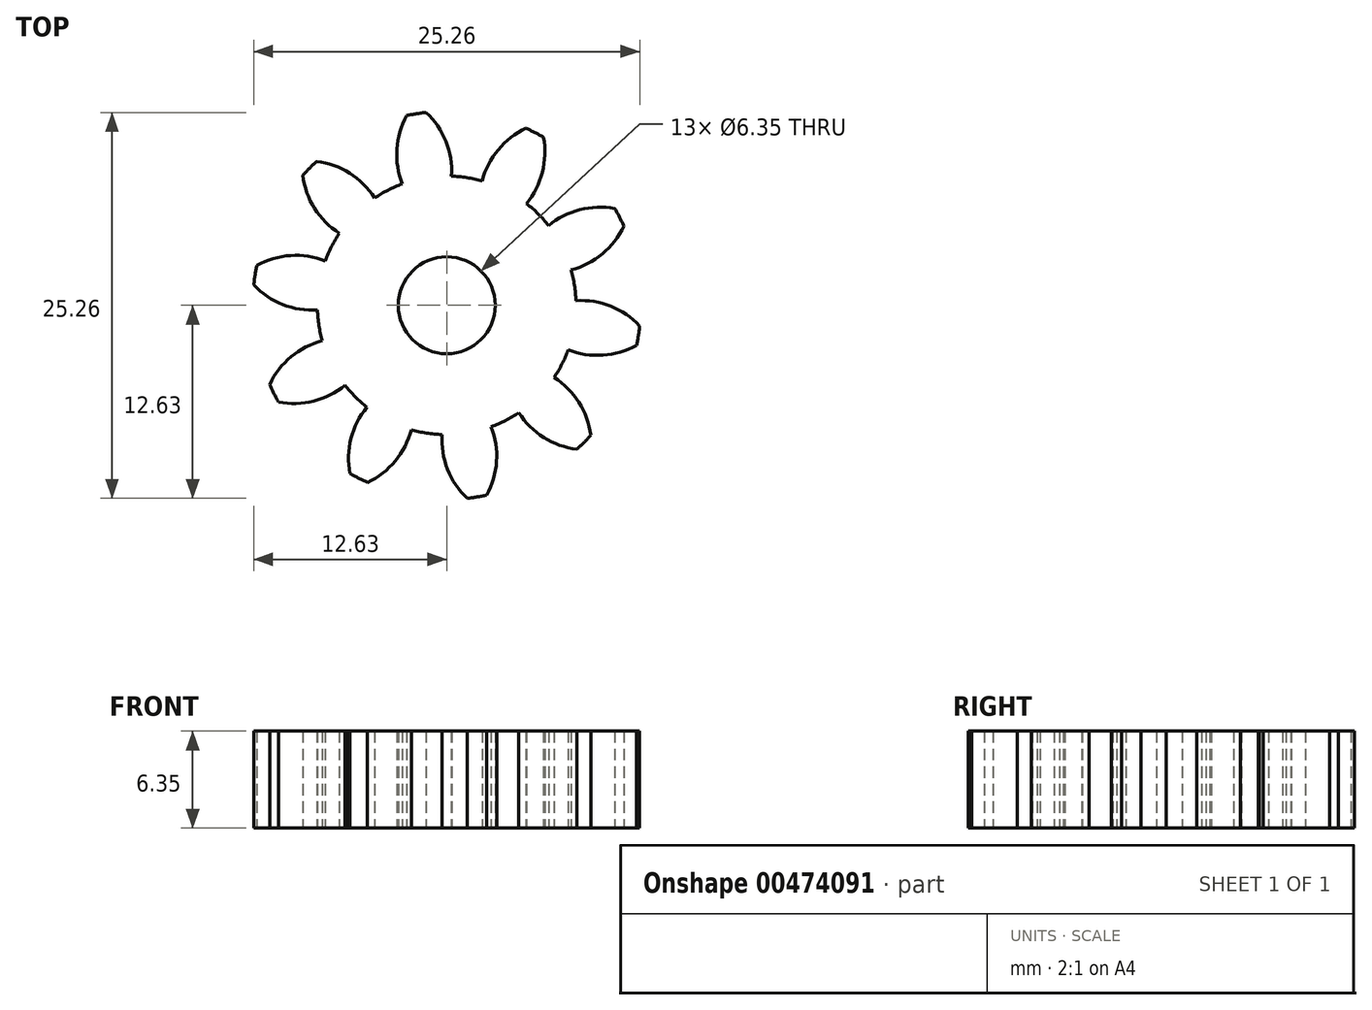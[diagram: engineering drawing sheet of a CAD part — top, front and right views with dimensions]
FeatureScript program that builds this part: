
annotation { "Feature Type Name" : "Feature", "Feature Type Description" : "" }
export const myFeature = defineFeature(function(context is Context, id is Id, definition is map)
    precondition{}
    {
        {
            var Q0;
            Q0=qCreatedBy(makeId("Top.planeOp"),FACE);
            var sketch = newSketch(context, id + "F0", { "sketchPlane" : qUnion([Q0])});
            skCircle(sketch, "E0", {"center": v(0, 0) * mm, "radius": 3.18 * mm});
            skCircle(sketch, "E1", {"center": v(0, 0) * mm, "radius": 8.47 * mm});
            skCircle(sketch, "E2", {"center": v(0, 0) * mm, "radius": 10.58 * mm, "construction": true});
            skCircle(sketch, "E3", {"center": v(0, 0) * mm, "radius": 12.7 * mm, "construction": true});
            skLineSegment(sketch, "E4", {"start": v(0, 0) * mm, "end": v(0, 10.58) * mm, "construction": true});
            skLineSegment(sketch, "E5", {"start": v(0, 10.58) * mm, "end": v(-16.23, 10.58) * mm, "construction": true});
            skLineSegment(sketch, "E6", {"start": v(0, 10.58) * mm, "end": v(-16.16, 4.7) * mm, "construction": true});
            skArc(sketch, "E7", {"start": v(0.3, 8.46) * mm, "mid": v(-0.06, 10.73) * mm, "end": v(-1.35, 12.63) * mm});
            skLineSegment(sketch, "E8", {"start": v(0, 0) * mm, "end": v(-1.99, 12.54) * mm, "construction": true});
            skArc(sketch, "E9.MirrorCS", {"start": v(-2.9, 7.95) * mm, "mid": v(-3.26, 10.22) * mm, "end": v(-2.62, 12.43) * mm});
            skArc(sketch, "E10", {"start": v(-1.35, 12.63) * mm, "mid": v(-1.99, 12.54) * mm, "end": v(-2.62, 12.43) * mm});
            skSolve(sketch);
        }
        {
            var Q0;
            Q0 = qSketchRegion(id + "F0", true);
            extrude(context, id + "F1", {"entities" : qUnion([Q0]), "depth" : 6.35 * mm});
        }
        {
            var Q0;
            Q0=makeQuery(id+"F1.opExtrude","SWEPT_FACE",FACE,{"disambiguationData":[OSD([sQuery(id+"F0.wireOp",EDGE,"E9.MirrorCS")])]});
            var Q1;
            Q1=makeQuery(id+"F1.opExtrude","SWEPT_FACE",FACE,{"disambiguationData":[OSD([sQuery(id+"F0.wireOp",EDGE,"HGqxILLp-dFeG-f2PO-mPlc-FlvlIbutgeJJ")])]});
            var Q2;
            Q2=makeQuery(id+"F1.opExtrude","SWEPT_FACE",FACE,{"disambiguationData":[OSD([sQuery(id+"F0.wireOp",EDGE,"E10")])]});
            var Q3;
            Q3=makeQuery(id+"F1.opExtrude","SWEPT_FACE",FACE,{"disambiguationData":[OSD([sQuery(id+"F0.wireOp",EDGE,"E7")])]});
            var Q4;
            Q4=makeQuery(id+"F1.opExtrude","SWEPT_FACE",FACE,{"disambiguationData":[OSD([sQuery(id+"F0.wireOp",EDGE,"uqKzqd37-BEkl-kbOT-yoQi-gvfLwq1ZGeWG")])]});
            var Q5;
            Q5=makeQuery(id+"F1.opExtrude","SWEPT_FACE",FACE,{"disambiguationData":[OSD([sQuery(id+"F0.wireOp",EDGE,"E1")])]});
            circularPattern(context, id + "F2", {"patternType" : PatternType.FACE, "faces" : qUnion([Q0, Q1, Q2, Q3, Q4]), "axis" : qUnion([Q5]), "angle" : 360 * degree, "instanceCount" : 10, "equalSpace" : true});
        }
    });
